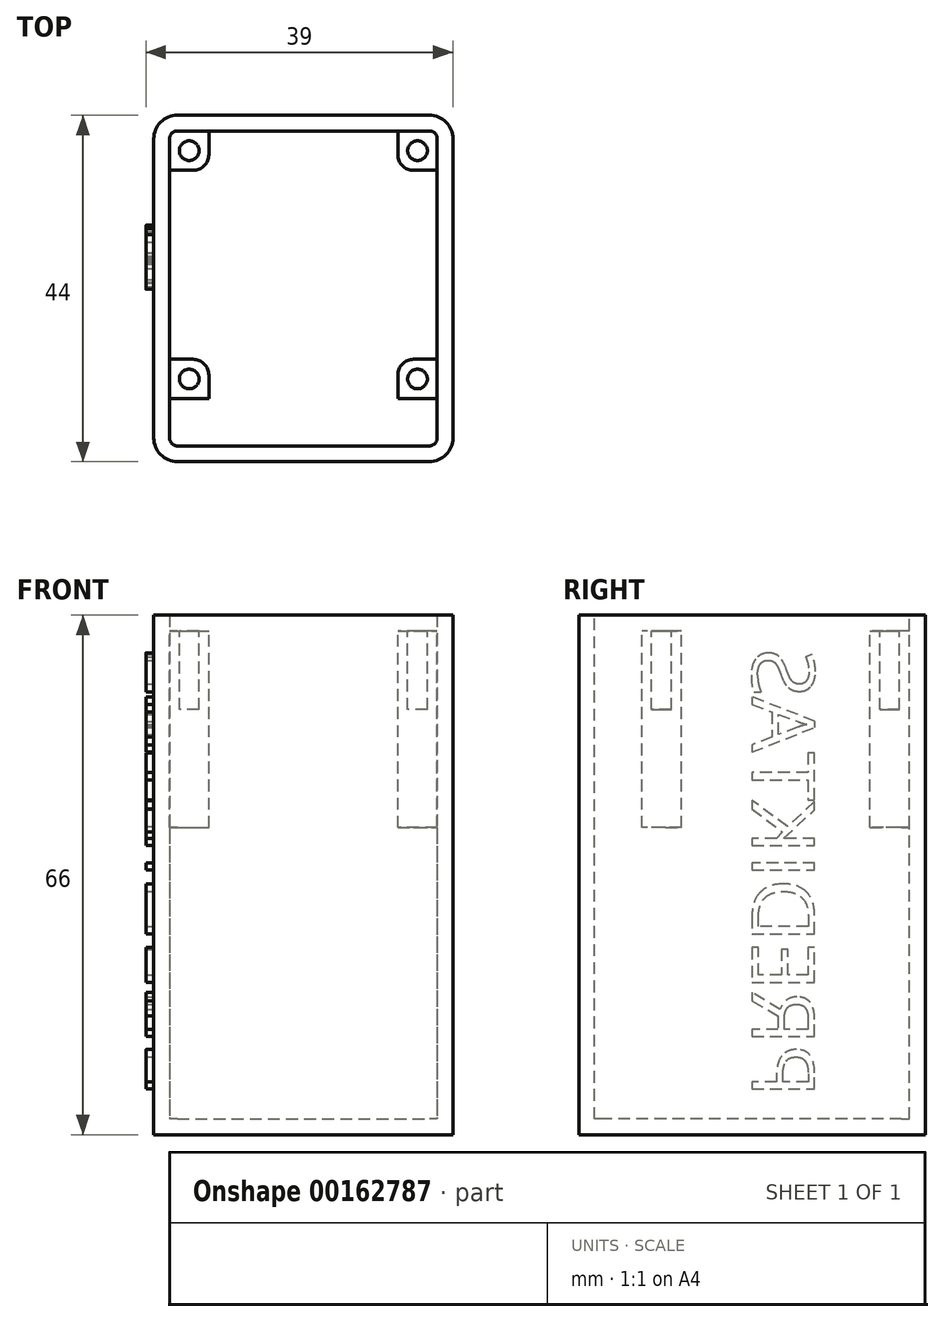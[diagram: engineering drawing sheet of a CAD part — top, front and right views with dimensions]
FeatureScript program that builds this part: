
annotation { "Feature Type Name" : "Feature", "Feature Type Description" : "" }
export const myFeature = defineFeature(function(context is Context, id is Id, definition is map)
    precondition{}
    {
        {
            var Q0;
            Q0=qCreatedBy(makeId("Top.planeOp"),FACE);
            var sketch = newSketch(context, id + "F0", { "sketchPlane" : qUnion([Q0])});
            skLineSegment(sketch, "E0.bottom", {"start": v(-16, 22) * mm, "end": v(16, 22) * mm});
            skLineSegment(sketch, "E0.top", {"start": v(-16, -22) * mm, "end": v(16, -22) * mm});
            skLineSegment(sketch, "E0.left", {"start": v(-19, 19) * mm, "end": v(-19, -19) * mm});
            skLineSegment(sketch, "E0.right", {"start": v(19, 19) * mm, "end": v(19, -19) * mm});
            skPoint(sketch, "E1.visualSharp", {"position": v(-19, 22) * mm});
            skArc(sketch, "E1.filletArc", {"start": v(-16, 22) * mm, "mid": v(-18.12, 21.12) * mm, "end": v(-19, 19) * mm});
            skPoint(sketch, "E2.visualSharp", {"position": v(19, 22) * mm});
            skArc(sketch, "E2.filletArc", {"start": v(19, 19) * mm, "mid": v(18.12, 21.12) * mm, "end": v(16, 22) * mm});
            skPoint(sketch, "E3.visualSharp", {"position": v(-19, -22) * mm});
            skArc(sketch, "E3.filletArc", {"start": v(-19, -19) * mm, "mid": v(-18.12, -21.12) * mm, "end": v(-16, -22) * mm});
            skPoint(sketch, "E4.visualSharp", {"position": v(19, -22) * mm});
            skArc(sketch, "E4.filletArc", {"start": v(16, -22) * mm, "mid": v(18.12, -21.12) * mm, "end": v(19, -19) * mm});
            skSolve(sketch);
        }
        {
            var Q0;
            Q0 = qSketchRegion(id + "F0", true);
            extrude(context, id + "F1", {"entities" : qUnion([Q0]), "depth" : 66 * mm, "offsetDistance" : 25 * mm});
        }
        {
            var Q0;
            Q0=makeQuery(id+"F1.opExtrude","CAP_FACE",FACE,{"disambiguationData":[OSD([sQuery(id+"F0.wireOp",EDGE,"E0.bottom"),sQuery(id+"F0.wireOp",EDGE,"E0.top"),sQuery(id+"F0.wireOp",EDGE,"E0.left"),sQuery(id+"F0.wireOp",EDGE,"E0.right"),sQuery(id+"F0.wireOp",EDGE,"E1.filletArc"),sQuery(id+"F0.wireOp",EDGE,"E2.filletArc"),sQuery(id+"F0.wireOp",EDGE,"E3.filletArc"),sQuery(id+"F0.wireOp",EDGE,"E4.filletArc")])],"isStart":false});
            shell(context, id + "F2", {"entities" : qUnion([Q0]), "thickness" : 2 * mm});
        }
        {
            var Q0;
            Q0=qCreatedBy(makeId("Top.planeOp"),FACE);
            cPlane(context, id + "F3", {"entities" : qUnion([Q0]), "cplaneType" : CPlaneType.OFFSET, "offset" : 64 * mm, "width" : 150 * mm, "height" : 150 * mm});
        }
        {
            var Q0;
            Q0=qCreatedBy(id+"F3.planeOp",FACE);
            var sketch = newSketch(context, id + "F4", { "sketchPlane" : qUnion([Q0])});
            skLineSegment(sketch, "E5.bottom", {"start": v(-17, 20) * mm, "end": v(-12, 20) * mm});
            skLineSegment(sketch, "E5.top", {"start": v(-17, 15) * mm, "end": v(-14, 15) * mm});
            skLineSegment(sketch, "E5.left", {"start": v(-17, 20) * mm, "end": v(-17, 15) * mm});
            skLineSegment(sketch, "E5.right", {"start": v(-12, 20) * mm, "end": v(-12, 17) * mm});
            skLineSegment(sketch, "E6.bottom", {"start": v(12, 20) * mm, "end": v(17, 20) * mm});
            skLineSegment(sketch, "E6.top", {"start": v(14, 15) * mm, "end": v(17, 15) * mm});
            skLineSegment(sketch, "E6.left", {"start": v(12, 20) * mm, "end": v(12, 17) * mm});
            skLineSegment(sketch, "E6.right", {"start": v(17, 20) * mm, "end": v(17, 15) * mm});
            skLineSegment(sketch, "E7.bottom", {"start": v(-17, -9) * mm, "end": v(-14, -9) * mm});
            skLineSegment(sketch, "E7.top", {"start": v(-17, -14) * mm, "end": v(-12, -14) * mm});
            skLineSegment(sketch, "E7.left", {"start": v(-17, -9) * mm, "end": v(-17, -14) * mm});
            skLineSegment(sketch, "E7.right", {"start": v(-12, -11) * mm, "end": v(-12, -14) * mm});
            skLineSegment(sketch, "E8.bottom", {"start": v(17, -9) * mm, "end": v(14, -9) * mm});
            skLineSegment(sketch, "E8.top", {"start": v(17, -14) * mm, "end": v(12, -14) * mm});
            skLineSegment(sketch, "E8.left", {"start": v(17, -9) * mm, "end": v(17, -14) * mm});
            skLineSegment(sketch, "E8.right", {"start": v(12, -11) * mm, "end": v(12, -14) * mm});
            skPoint(sketch, "E9.visualSharp", {"position": v(-12, 15) * mm});
            skArc(sketch, "E9.filletArc", {"start": v(-14, 15) * mm, "mid": v(-12.59, 15.59) * mm, "end": v(-12, 17) * mm});
            skPoint(sketch, "E10.visualSharp", {"position": v(12, 15) * mm});
            skArc(sketch, "E10.filletArc", {"start": v(12, 17) * mm, "mid": v(12.59, 15.59) * mm, "end": v(14, 15) * mm});
            skPoint(sketch, "E11.visualSharp", {"position": v(-12, -9) * mm});
            skArc(sketch, "E11.filletArc", {"start": v(-12, -11) * mm, "mid": v(-12.59, -9.59) * mm, "end": v(-14, -9) * mm});
            skPoint(sketch, "E12.visualSharp", {"position": v(12, -9) * mm});
            skArc(sketch, "E12.filletArc", {"start": v(14, -9) * mm, "mid": v(12.59, -9.59) * mm, "end": v(12, -11) * mm});
            skSolve(sketch);
        }
        {
            var Q0;
            Q0 = qSketchRegion(id + "F4", true);
            extrude(context, id + "F5", {"entities" : qUnion([Q0]), "operationType" : NewBodyOperationType.ADD, "oppositeDirection" : true, "depth" : 25 * mm, "offsetDistance" : 25 * mm});
        }
        {
            var Q0;
            Q0=makeQuery(id+"F5.opExtrude","CAP_FACE",FACE,{"disambiguationData":[OSD([sQuery(id+"F4.wireOp",EDGE,"E5.bottom"),sQuery(id+"F4.wireOp",EDGE,"E5.top"),sQuery(id+"F4.wireOp",EDGE,"E5.left"),sQuery(id+"F4.wireOp",EDGE,"E5.right"),sQuery(id+"F4.wireOp",EDGE,"E9.filletArc")])],"isStart":true});
            var sketch = newSketch(context, id + "F6", { "sketchPlane" : qUnion([Q0])});
            skCircle(sketch, "E13", {"center": v(-14.5, 17.5) * mm, "radius": 1.25 * mm});
            skCircle(sketch, "E14", {"center": v(14.5, 17.5) * mm, "radius": 1.25 * mm});
            skCircle(sketch, "E15", {"center": v(-14.5, -11.5) * mm, "radius": 1.25 * mm});
            skCircle(sketch, "E16", {"center": v(14.5, -11.5) * mm, "radius": 1.25 * mm});
            skSolve(sketch);
        }
        {
            var Q0;
            Q0 = qSketchRegion(id + "F6", true);
            extrude(context, id + "F7", {"entities" : qUnion([Q0]), "operationType" : NewBodyOperationType.REMOVE, "oppositeDirection" : true, "depth" : 10 * mm, "offsetDistance" : 25 * mm});
        }
        {
            var Q0;
            Q0=makeQuery(id+"F1.opExtrude","SWEPT_FACE",FACE,{"disambiguationData":[OSD([sQuery(id+"F0.wireOp",EDGE,"E0.left")])]});
            var sketch = newSketch(context, id + "F8", { "sketchPlane" : qUnion([Q0])});
            skText(sketch, "E17", { "text": "PREDIKTAS", "fontName": "OpenSans-Regular.ttf"});
            const initialGuessF8  = {"E17": [0, 0.0047, 0, 1, 0.008]};
            skSetInitialGuess(sketch, initialGuessF8);
            skSolve(sketch);
        }
        {
            var Q0;
            Q0 = qSketchRegion(id + "F8", true);
            extrude(context, id + "F9", {"entities" : qUnion([Q0]), "operationType" : NewBodyOperationType.ADD, "depth" : 1 * mm, "offsetDistance" : 25 * mm});
        }
    });
